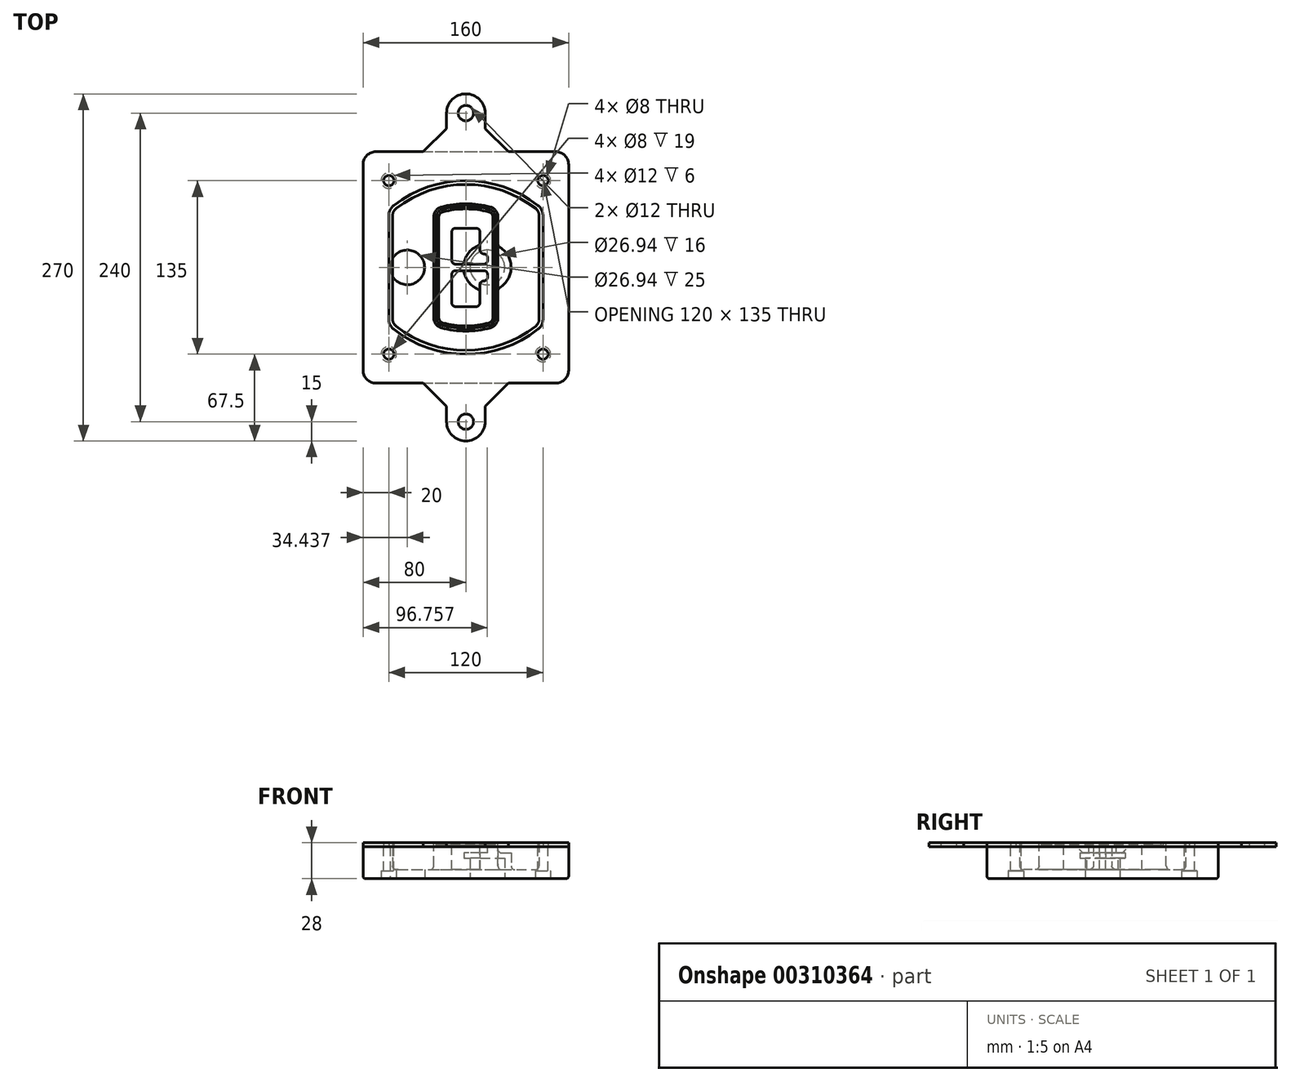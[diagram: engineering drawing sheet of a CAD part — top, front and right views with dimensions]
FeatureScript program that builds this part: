
annotation { "Feature Type Name" : "Feature", "Feature Type Description" : "" }
export const myFeature = defineFeature(function(context is Context, id is Id, definition is map)
    precondition{}
    {
        {
            var Q0;
            Q0=qCreatedBy(makeId("Top.planeOp"),FACE);
            var sketch = newSketch(context, id + "F0", { "sketchPlane" : qUnion([Q0])});
            skPoint(sketch, "E0.rect.middle", {"position": v(0, 0) * mm});
            skLineSegment(sketch, "E1.bottom", {"start": v(-70, -90) * mm, "end": v(70, -90) * mm});
            skLineSegment(sketch, "E1.top", {"start": v(-70, 90) * mm, "end": v(70, 90) * mm});
            skLineSegment(sketch, "E1.left", {"start": v(-80, -80) * mm, "end": v(-80, 80) * mm});
            skLineSegment(sketch, "E1.right", {"start": v(80, -80) * mm, "end": v(80, 80) * mm});
            skLineSegment(sketch, "E2", {"start": v(-80, 90) * mm, "end": v(80, -90) * mm, "construction": true});
            skLineSegment(sketch, "E3", {"start": v(80, 90) * mm, "end": v(-80, -90) * mm, "construction": true});
            skCircle(sketch, "E4", {"center": v(-60, 67.5) * mm, "radius": 4 * mm});
            skCircle(sketch, "E5", {"center": v(60, 67.5) * mm, "radius": 4 * mm});
            skCircle(sketch, "E6", {"center": v(60, -67.5) * mm, "radius": 4 * mm});
            skCircle(sketch, "E7", {"center": v(-60, -67.5) * mm, "radius": 4 * mm});
            skLineSegment(sketch, "E8", {"start": v(-60, 67.5) * mm, "end": v(60, 67.5) * mm, "construction": true});
            skLineSegment(sketch, "E9", {"start": v(60, 67.5) * mm, "end": v(60, -67.5) * mm, "construction": true});
            skLineSegment(sketch, "E10", {"start": v(60, -67.5) * mm, "end": v(-60, -67.5) * mm, "construction": true});
            skLineSegment(sketch, "E11", {"start": v(-60, -67.5) * mm, "end": v(-60, 67.5) * mm, "construction": true});
            skLineSegment(sketch, "E12", {"start": v(-60, 40.3) * mm, "end": v(-60, -40.3) * mm});
            skLineSegment(sketch, "E13", {"start": v(60, 40.3) * mm, "end": v(60, -40.3) * mm});
            skArc(sketch, "E14", {"start": v(56.15, 48.18) * mm, "mid": v(0, 67.5) * mm, "end": v(-56.15, 48.18) * mm});
            skArc(sketch, "E15", {"start": v(-56.15, -48.18) * mm, "mid": v(0, -67.5) * mm, "end": v(56.15, -48.18) * mm});
            skLineSegment(sketch, "E16", {"start": v(-60, 0) * mm, "end": v(60, 0) * mm, "construction": true});
            skPoint(sketch, "E17.visualSharp", {"position": v(-60, -45) * mm});
            skArc(sketch, "E17.filletArc", {"start": v(-60, -40.3) * mm, "mid": v(-58.99, -44.68) * mm, "end": v(-56.15, -48.18) * mm});
            skPoint(sketch, "E18.visualSharp", {"position": v(-60, 45) * mm});
            skArc(sketch, "E18.filletArc", {"start": v(-56.15, 48.18) * mm, "mid": v(-58.99, 44.68) * mm, "end": v(-60, 40.3) * mm});
            skPoint(sketch, "E19.visualSharp", {"position": v(60, 45) * mm});
            skArc(sketch, "E19.filletArc", {"start": v(60, 40.3) * mm, "mid": v(58.99, 44.68) * mm, "end": v(56.15, 48.18) * mm});
            skPoint(sketch, "E20.visualSharp", {"position": v(60, -45) * mm});
            skArc(sketch, "E20.filletArc", {"start": v(56.15, -48.18) * mm, "mid": v(58.99, -44.68) * mm, "end": v(60, -40.3) * mm});
            skPoint(sketch, "E21.visualSharp", {"position": v(-80, 90) * mm});
            skArc(sketch, "E21.filletArc", {"start": v(-70, 90) * mm, "mid": v(-77.07, 87.07) * mm, "end": v(-80, 80) * mm});
            skPoint(sketch, "E22.visualSharp", {"position": v(80, 90) * mm});
            skArc(sketch, "E22.filletArc", {"start": v(80, 80) * mm, "mid": v(77.07, 87.07) * mm, "end": v(70, 90) * mm});
            skPoint(sketch, "E23.visualSharp", {"position": v(80, -90) * mm});
            skArc(sketch, "E23.filletArc", {"start": v(70, -90) * mm, "mid": v(77.07, -87.07) * mm, "end": v(80, -80) * mm});
            skPoint(sketch, "E24.visualSharp", {"position": v(-80, -90) * mm});
            skArc(sketch, "E24.filletArc", {"start": v(-80, -80) * mm, "mid": v(-77.07, -87.07) * mm, "end": v(-70, -90) * mm});
            skArc(sketch, "E25.0", {"start": v(57, 40.3) * mm, "mid": v(56.3, 43.36) * mm, "end": v(54.3, 45.81) * mm});
            skLineSegment(sketch, "E25.1", {"start": v(57, 40.3) * mm, "end": v(57, -40.3) * mm});
            skArc(sketch, "E25.2", {"start": v(54.3, -45.81) * mm, "mid": v(56.3, -43.36) * mm, "end": v(57, -40.3) * mm});
            skArc(sketch, "E25.3", {"start": v(-54.3, -45.81) * mm, "mid": v(0, -64.5) * mm, "end": v(54.3, -45.81) * mm});
            skArc(sketch, "E25.4", {"start": v(-57, -40.3) * mm, "mid": v(-56.3, -43.36) * mm, "end": v(-54.3, -45.81) * mm});
            skArc(sketch, "E25.5", {"start": v(54.3, 45.81) * mm, "mid": v(0, 64.5) * mm, "end": v(-54.3, 45.81) * mm});
            skLineSegment(sketch, "E25.6", {"start": v(-57, 40.3) * mm, "end": v(-57, -40.3) * mm});
            skArc(sketch, "E25.7", {"start": v(-54.3, 45.81) * mm, "mid": v(-56.3, 43.36) * mm, "end": v(-57, 40.3) * mm});
            skArc(sketch, "E26.0", {"start": v(-58.62, 51.33) * mm, "mid": v(-62.58, 46.43) * mm, "end": v(-64, 40.3) * mm});
            skArc(sketch, "E26.1", {"start": v(58.62, 51.33) * mm, "mid": v(0, 71.5) * mm, "end": v(-58.62, 51.33) * mm});
            skArc(sketch, "E26.2", {"start": v(64, 40.3) * mm, "mid": v(62.58, 46.43) * mm, "end": v(58.62, 51.33) * mm});
            skLineSegment(sketch, "E26.3", {"start": v(64, 40.3) * mm, "end": v(64, -40.3) * mm});
            skArc(sketch, "E26.4", {"start": v(58.62, -51.33) * mm, "mid": v(62.58, -46.43) * mm, "end": v(64, -40.3) * mm});
            skLineSegment(sketch, "E26.5", {"start": v(-64, 40.3) * mm, "end": v(-64, -40.3) * mm});
            skArc(sketch, "E26.6", {"start": v(-58.62, -51.33) * mm, "mid": v(0, -71.5) * mm, "end": v(58.62, -51.33) * mm});
            skArc(sketch, "E26.7", {"start": v(-64, -40.3) * mm, "mid": v(-62.58, -46.43) * mm, "end": v(-58.62, -51.33) * mm});
            skSolve(sketch);
        }
        {
            var Q0;
            Q0=makeQuery(id+"F0.imprint","IMPRINT",FACE,{"disambiguationData":[TD([[makeQuery(id+"F0.imprint","IMPRINT",EDGE,{"derivedFrom":sQuery(id+"F0.wireOp",EDGE,"E1.bottom")}),1.0]])]});
            var Q1;
            Q1=makeQuery(id+"F0.imprint","IMPRINT",FACE,{"disambiguationData":[TD([[makeQuery(id+"F0.imprint","IMPRINT",EDGE,{"derivedFrom":sQuery(id+"F0.wireOp",EDGE,"E12")}),1.0]])]});
            var Q2;
            Q2=makeQuery(id+"F0.imprint","IMPRINT",FACE,{"disambiguationData":[TD([[makeQuery(id+"F0.imprint","IMPRINT",EDGE,{"derivedFrom":sQuery(id+"F0.wireOp",EDGE,"E25.0")}),1.0]])]});
            var Q3;
            Q3=makeQuery(id+"F0.imprint","IMPRINT",FACE,{"disambiguationData":[TD([[makeQuery(id+"F0.imprint","IMPRINT",EDGE,{"derivedFrom":sQuery(id+"F0.wireOp",EDGE,"E12")}),-1.0]])]});
            extrude(context, id + "F1", {"entities" : qUnion([Q0, Q1, Q2, Q3]), "oppositeDirection" : true, "depth" : 25 * mm});
        }
        {
            var Q0;
            Q0=makeQuery(id+"F0.imprint","IMPRINT",FACE,{"disambiguationData":[TD([[makeQuery(id+"F0.imprint","IMPRINT",EDGE,{"derivedFrom":sQuery(id+"F0.wireOp",EDGE,"E12")}),1.0]])]});
            extrude(context, id + "F2", {"entities" : qUnion([Q0]), "operationType" : NewBodyOperationType.ADD, "depth" : 3 * mm});
        }
        {
            var Q0;
            Q0=makeQuery(id+"F0.imprint","IMPRINT",FACE,{"disambiguationData":[TD([[makeQuery(id+"F0.imprint","IMPRINT",EDGE,{"derivedFrom":sQuery(id+"F0.wireOp",EDGE,"E25.0")}),1.0]])]});
            extrude(context, id + "F3", {"entities" : qUnion([Q0]), "operationType" : NewBodyOperationType.REMOVE, "oppositeDirection" : true, "depth" : 18 * mm});
        }
        {
            var Q0;
            Q0=makeQuery(id+"F2.opExtrude","CAP_FACE",FACE,{"disambiguationData":[OSD([sQuery(id+"F0.wireOp",EDGE,"E12"),sQuery(id+"F0.wireOp",EDGE,"E13"),sQuery(id+"F0.wireOp",EDGE,"E14"),sQuery(id+"F0.wireOp",EDGE,"E15"),sQuery(id+"F0.wireOp",EDGE,"E17.filletArc"),sQuery(id+"F0.wireOp",EDGE,"E18.filletArc"),sQuery(id+"F0.wireOp",EDGE,"E19.filletArc"),sQuery(id+"F0.wireOp",EDGE,"E20.filletArc"),sQuery(id+"F0.wireOp",EDGE,"E25.0"),sQuery(id+"F0.wireOp",EDGE,"E25.1"),sQuery(id+"F0.wireOp",EDGE,"E25.2"),sQuery(id+"F0.wireOp",EDGE,"E25.3"),sQuery(id+"F0.wireOp",EDGE,"E25.4"),sQuery(id+"F0.wireOp",EDGE,"E25.5"),sQuery(id+"F0.wireOp",EDGE,"E25.6"),sQuery(id+"F0.wireOp",EDGE,"E25.7")])],"isStart":false});
            var sketch = newSketch(context, id + "F4", { "sketchPlane" : qUnion([Q0])});
            skArc(sketch, "E27.0", {"start": v(-19.08, -46.97) * mm, "mid": v(0, -49.5) * mm, "end": v(19.08, -46.97) * mm});
            skArc(sketch, "E28.0", {"start": v(19.08, 46.97) * mm, "mid": v(0, 49.5) * mm, "end": v(-19.08, 46.97) * mm});
            skLineSegment(sketch, "E29", {"start": v(-25, 39.25) * mm, "end": v(-25, -39.25) * mm});
            skLineSegment(sketch, "E30", {"start": v(25, 39.25) * mm, "end": v(25, -39.25) * mm});
            skLineSegment(sketch, "E31", {"start": v(-25, 45.1) * mm, "end": v(25, 45.1) * mm, "construction": true});
            skLineSegment(sketch, "E32", {"start": v(-25, -45.1) * mm, "end": v(25, -45.1) * mm, "construction": true});
            skPoint(sketch, "E33.visualSharp", {"position": v(-25, 45.1) * mm});
            skArc(sketch, "E33.filletArc", {"start": v(-19.08, 46.97) * mm, "mid": v(-23.35, 44.11) * mm, "end": v(-25, 39.25) * mm});
            skPoint(sketch, "E34.visualSharp", {"position": v(25, 45.1) * mm});
            skArc(sketch, "E34.filletArc", {"start": v(25, 39.25) * mm, "mid": v(23.35, 44.11) * mm, "end": v(19.08, 46.97) * mm});
            skPoint(sketch, "E35.visualSharp", {"position": v(25, -45.1) * mm});
            skArc(sketch, "E35.filletArc", {"start": v(19.08, -46.97) * mm, "mid": v(23.35, -44.11) * mm, "end": v(25, -39.25) * mm});
            skPoint(sketch, "E36.visualSharp", {"position": v(-25, -45.1) * mm});
            skArc(sketch, "E36.filletArc", {"start": v(-25, -39.25) * mm, "mid": v(-23.35, -44.11) * mm, "end": v(-19.08, -46.97) * mm});
            skArc(sketch, "E37.0", {"start": v(54.3, 45.81) * mm, "mid": v(0, 64.5) * mm, "end": v(-54.3, 45.81) * mm});
            skArc(sketch, "E37.1", {"start": v(-54.3, 45.81) * mm, "mid": v(-56.3, 43.36) * mm, "end": v(-57, 40.3) * mm});
            skLineSegment(sketch, "E37.2", {"start": v(-57, 40.3) * mm, "end": v(-57, -40.3) * mm});
            skArc(sketch, "E37.3", {"start": v(-57, -40.3) * mm, "mid": v(-56.3, -43.36) * mm, "end": v(-54.3, -45.81) * mm});
            skArc(sketch, "E37.4", {"start": v(-54.3, -45.81) * mm, "mid": v(0, -64.5) * mm, "end": v(54.3, -45.81) * mm});
            skArc(sketch, "E37.5", {"start": v(54.3, -45.81) * mm, "mid": v(56.3, -43.36) * mm, "end": v(57, -40.3) * mm});
            skLineSegment(sketch, "E37.6", {"start": v(57, 40.3) * mm, "end": v(57, -40.3) * mm});
            skArc(sketch, "E37.7", {"start": v(57, 40.3) * mm, "mid": v(56.3, 43.36) * mm, "end": v(54.3, 45.81) * mm});
            skLineSegment(sketch, "E38.0", {"start": v(23, 39.25) * mm, "end": v(23, -39.25) * mm});
            skArc(sketch, "E38.1", {"start": v(18.56, -45.04) * mm, "mid": v(21.76, -42.9) * mm, "end": v(23, -39.25) * mm});
            skArc(sketch, "E38.2", {"start": v(-18.56, -45.04) * mm, "mid": v(0, -47.5) * mm, "end": v(18.56, -45.04) * mm});
            skArc(sketch, "E38.3", {"start": v(-23, -39.25) * mm, "mid": v(-21.76, -42.9) * mm, "end": v(-18.56, -45.04) * mm});
            skLineSegment(sketch, "E38.4", {"start": v(-23, 39.25) * mm, "end": v(-23, -39.25) * mm});
            skArc(sketch, "E38.5", {"start": v(23, 39.25) * mm, "mid": v(21.76, 42.9) * mm, "end": v(18.56, 45.04) * mm});
            skArc(sketch, "E38.6", {"start": v(-18.56, 45.04) * mm, "mid": v(-21.76, 42.9) * mm, "end": v(-23, 39.25) * mm});
            skArc(sketch, "E38.7", {"start": v(18.56, 45.04) * mm, "mid": v(0, 47.5) * mm, "end": v(-18.56, 45.04) * mm});
            skArc(sketch, "E39.0", {"start": v(21, 39.25) * mm, "mid": v(20.18, 41.68) * mm, "end": v(18.04, 43.1) * mm});
            skLineSegment(sketch, "E39.1", {"start": v(21, 39.25) * mm, "end": v(21, -39.25) * mm});
            skArc(sketch, "E39.2", {"start": v(18.04, -43.1) * mm, "mid": v(20.18, -41.68) * mm, "end": v(21, -39.25) * mm});
            skArc(sketch, "E39.3", {"start": v(-18.04, -43.1) * mm, "mid": v(0, -45.5) * mm, "end": v(18.04, -43.1) * mm});
            skArc(sketch, "E39.4", {"start": v(-21, -39.25) * mm, "mid": v(-20.18, -41.68) * mm, "end": v(-18.04, -43.1) * mm});
            skArc(sketch, "E39.5", {"start": v(18.04, 43.1) * mm, "mid": v(0, 45.5) * mm, "end": v(-18.04, 43.1) * mm});
            skLineSegment(sketch, "E39.6", {"start": v(-21, 39.25) * mm, "end": v(-21, -39.25) * mm});
            skArc(sketch, "E39.7", {"start": v(-18.04, 43.1) * mm, "mid": v(-20.18, 41.68) * mm, "end": v(-21, 39.25) * mm});
            skLineSegment(sketch, "E40", {"start": v(-25, 0) * mm, "end": v(25, 0) * mm, "construction": true});
            skLineSegment(sketch, "E41", {"start": v(-11, 5.5) * mm, "end": v(-11, 27.5) * mm});
            skLineSegment(sketch, "E42", {"start": v(-8, 30.5) * mm, "end": v(8, 30.5) * mm});
            skLineSegment(sketch, "E43", {"start": v(11, 27.5) * mm, "end": v(11, 13.5) * mm});
            skLineSegment(sketch, "E44", {"start": v(14, 10.5) * mm, "end": v(14, 10.5) * mm});
            skLineSegment(sketch, "E45", {"start": v(17, 7.5) * mm, "end": v(17, 5.5) * mm});
            skLineSegment(sketch, "E46", {"start": v(14, 2.5) * mm, "end": v(-8, 2.5) * mm});
            skPoint(sketch, "E47.visualSharp", {"position": v(-11, 30.5) * mm});
            skArc(sketch, "E47.filletArc", {"start": v(-8, 30.5) * mm, "mid": v(-10.12, 29.62) * mm, "end": v(-11, 27.5) * mm});
            skPoint(sketch, "E48.visualSharp", {"position": v(11, 30.5) * mm});
            skArc(sketch, "E48.filletArc", {"start": v(11, 27.5) * mm, "mid": v(10.12, 29.62) * mm, "end": v(8, 30.5) * mm});
            skPoint(sketch, "E49.visualSharp", {"position": v(11, 10.5) * mm});
            skArc(sketch, "E49.filletArc", {"start": v(11, 13.5) * mm, "mid": v(11.88, 11.38) * mm, "end": v(14, 10.5) * mm});
            skPoint(sketch, "E50.visualSharp", {"position": v(17, 10.5) * mm});
            skArc(sketch, "E50.filletArc", {"start": v(17, 7.5) * mm, "mid": v(16.12, 9.62) * mm, "end": v(14, 10.5) * mm});
            skPoint(sketch, "E51.visualSharp", {"position": v(17, 2.5) * mm});
            skArc(sketch, "E51.filletArc", {"start": v(14, 2.5) * mm, "mid": v(16.12, 3.38) * mm, "end": v(17, 5.5) * mm});
            skPoint(sketch, "E52.visualSharp", {"position": v(-11, 2.5) * mm});
            skArc(sketch, "E52.filletArc", {"start": v(-11, 5.5) * mm, "mid": v(-10.12, 3.38) * mm, "end": v(-8, 2.5) * mm});
            skLineSegment(sketch, "E53.0.MirrorCS", {"start": v(14, -2.5) * mm, "end": v(-8, -2.5) * mm});
            skArc(sketch, "E54.0.MirrorCS", {"start": v(-11, -5.5) * mm, "mid": v(-10.12, -3.38) * mm, "end": v(-8, -2.5) * mm});
            skLineSegment(sketch, "E55.0.MirrorCS", {"start": v(-11, -5.5) * mm, "end": v(-11, -27.5) * mm});
            skArc(sketch, "E56.0.MirrorCS", {"start": v(-8, -30.5) * mm, "mid": v(-10.12, -29.62) * mm, "end": v(-11, -27.5) * mm});
            skLineSegment(sketch, "E57.0.MirrorCS", {"start": v(-8, -30.5) * mm, "end": v(8, -30.5) * mm});
            skArc(sketch, "E58.0.MirrorCS", {"start": v(11, -27.5) * mm, "mid": v(10.12, -29.62) * mm, "end": v(8, -30.5) * mm});
            skLineSegment(sketch, "E59.0.MirrorCS", {"start": v(11, -27.5) * mm, "end": v(11, -13.5) * mm});
            skArc(sketch, "E60.0.MirrorCS", {"start": v(11, -13.5) * mm, "mid": v(11.88, -11.38) * mm, "end": v(14, -10.5) * mm});
            skArc(sketch, "E61.0.MirrorCS", {"start": v(17, -7.5) * mm, "mid": v(16.12, -9.62) * mm, "end": v(14, -10.5) * mm});
            skLineSegment(sketch, "E62.0.MirrorCS", {"start": v(17, -7.5) * mm, "end": v(17, -5.5) * mm});
            skArc(sketch, "E63.0.MirrorCS", {"start": v(14, -2.5) * mm, "mid": v(16.12, -3.38) * mm, "end": v(17, -5.5) * mm});
            skSolve(sketch);
        }
        {
            var Q0;
            Q0=makeQuery(id+"F4.imprint","IMPRINT",FACE,{"disambiguationData":[TD([[makeQuery(id+"F4.imprint","IMPRINT",EDGE,{"derivedFrom":sQuery(id+"F4.wireOp",EDGE,"E27.0")}),1.0]])]});
            var Q1;
            Q1=makeQuery(id+"F4.imprint","IMPRINT",FACE,{"disambiguationData":[TD([[makeQuery(id+"F4.imprint","IMPRINT",EDGE,{"derivedFrom":sQuery(id+"F4.wireOp",EDGE,"E38.0")}),-1.0]])]});
            var Q2;
            Q2=makeQuery(id+"F4.imprint","IMPRINT",FACE,{"disambiguationData":[TD([[makeQuery(id+"F4.imprint","IMPRINT",EDGE,{"derivedFrom":sQuery(id+"F4.wireOp",EDGE,"E39.0")}),1.0]])]});
            extrude(context, id + "F5", {"entities" : qUnion([Q0, Q1, Q2]), "operationType" : NewBodyOperationType.ADD, "endBound" : BoundingType.UP_TO_NEXT, "oppositeDirection" : true, "depth" : 25 * mm});
        }
        {
            var Q0;
            Q0=makeQuery(id+"F4.imprint","IMPRINT",FACE,{"disambiguationData":[TD([[makeQuery(id+"F4.imprint","IMPRINT",EDGE,{"derivedFrom":sQuery(id+"F4.wireOp",EDGE,"E38.0")}),-1.0]])]});
            extrude(context, id + "F6", {"entities" : qUnion([Q0]), "operationType" : NewBodyOperationType.REMOVE, "oppositeDirection" : true, "depth" : 2 * mm});
        }
        {
            var Q0;
            Q0=makeQuery(id+"F1.opExtrude","CAP_FACE",FACE,{"disambiguationData":[OSD([sQuery(id+"F0.wireOp",EDGE,"E1.bottom"),sQuery(id+"F0.wireOp",EDGE,"E1.top"),sQuery(id+"F0.wireOp",EDGE,"E1.left"),sQuery(id+"F0.wireOp",EDGE,"E1.right"),sQuery(id+"F0.wireOp",EDGE,"E4"),sQuery(id+"F0.wireOp",EDGE,"E5"),sQuery(id+"F0.wireOp",EDGE,"E6"),sQuery(id+"F0.wireOp",EDGE,"E7"),sQuery(id+"F0.wireOp",EDGE,"E21.filletArc"),sQuery(id+"F0.wireOp",EDGE,"E22.filletArc"),sQuery(id+"F0.wireOp",EDGE,"E23.filletArc"),sQuery(id+"F0.wireOp",EDGE,"E24.filletArc")])],"isStart":false});
            var sketch = newSketch(context, id + "F7", { "sketchPlane" : qUnion([Q0])});
            skCircle(sketch, "E64", {"center": v(16.76, 0) * mm, "radius": 13.47 * mm});
            skCircle(sketch, "E65", {"center": v(-45.56, 0) * mm, "radius": 13.47 * mm});
            skLineSegment(sketch, "E66", {"start": v(80, 0) * mm, "end": v(-80, 0) * mm});
            skCircle(sketch, "E67", {"center": v(16.76, 0) * mm, "radius": 18.47 * mm});
            skCircle(sketch, "E68", {"center": v(60, -67.5) * mm, "radius": 6 * mm});
            skCircle(sketch, "E69", {"center": v(-60, -67.5) * mm, "radius": 6 * mm});
            skCircle(sketch, "E70", {"center": v(-60, 67.5) * mm, "radius": 6 * mm});
            skCircle(sketch, "E71", {"center": v(60, 67.5) * mm, "radius": 6 * mm});
            skSolve(sketch);
        }
        {
            var Q0;
            {var subQ1=sQuery(id+"F7.wireOp",EDGE,"E66");var subQ4=sQuery(id+"F7.wireOp",EDGE,"E64");var subQ6=makeQuery(id+"F7.imprint","INTERSECT",VERTEX,{"disambiguationData":[OD(0.0)],"derivedFrom":[subQ4,subQ1]});Q0=makeQuery(id+"F7.imprint","IMPRINT",FACE,{"disambiguationData":[TD([[makeQuery(id+"F7.imprint","IMPRINT",EDGE,{"disambiguationData":[TD([[subQ6,-1.0]])],"derivedFrom":subQ4}),-1.0]])]});}
            var Q1;
            {var subQ0=sQuery(id+"F7.wireOp",EDGE,"E66");var subQ1=sQuery(id+"F7.wireOp",EDGE,"E64");var subQ3=makeQuery(id+"F7.imprint","INTERSECT",VERTEX,{"disambiguationData":[OD(0.0)],"derivedFrom":[subQ1,subQ0]});Q1=makeQuery(id+"F7.imprint","IMPRINT",FACE,{"disambiguationData":[TD([[makeQuery(id+"F7.imprint","IMPRINT",EDGE,{"disambiguationData":[TD([[subQ3,-1.0]])],"derivedFrom":subQ1}),1.0]])]});}
            var Q2;
            {var subQ0=sQuery(id+"F7.wireOp",EDGE,"E66");var subQ1=sQuery(id+"F7.wireOp",EDGE,"E64");var subQ3=makeQuery(id+"F7.imprint","INTERSECT",VERTEX,{"disambiguationData":[OD(0.0)],"derivedFrom":[subQ1,subQ0]});Q2=makeQuery(id+"F7.imprint","IMPRINT",FACE,{"disambiguationData":[TD([[makeQuery(id+"F7.imprint","IMPRINT",EDGE,{"disambiguationData":[TD([[subQ3,1.0]])],"derivedFrom":subQ1}),1.0]])]});}
            var Q3;
            {var subQ1=sQuery(id+"F7.wireOp",EDGE,"E66");var subQ4=sQuery(id+"F7.wireOp",EDGE,"E64");var subQ6=makeQuery(id+"F7.imprint","INTERSECT",VERTEX,{"disambiguationData":[OD(0.0)],"derivedFrom":[subQ4,subQ1]});Q3=makeQuery(id+"F7.imprint","IMPRINT",FACE,{"disambiguationData":[TD([[makeQuery(id+"F7.imprint","IMPRINT",EDGE,{"disambiguationData":[TD([[subQ6,1.0]])],"derivedFrom":subQ4}),-1.0]])]});}
            extrude(context, id + "F8", {"entities" : qUnion([Q0, Q1, Q2, Q3]), "operationType" : NewBodyOperationType.ADD, "oppositeDirection" : true, "depth" : 20 * mm});
        }
        {
            var Q0;
            {var subQ0=sQuery(id+"F7.wireOp",EDGE,"E66");var subQ1=sQuery(id+"F7.wireOp",EDGE,"E64");var subQ3=makeQuery(id+"F7.imprint","INTERSECT",VERTEX,{"disambiguationData":[OD(0.0)],"derivedFrom":[subQ1,subQ0]});Q0=makeQuery(id+"F7.imprint","IMPRINT",FACE,{"disambiguationData":[TD([[makeQuery(id+"F7.imprint","IMPRINT",EDGE,{"disambiguationData":[TD([[subQ3,-1.0]])],"derivedFrom":subQ1}),1.0]])]});}
            var Q1;
            {var subQ0=sQuery(id+"F7.wireOp",EDGE,"E66");var subQ1=sQuery(id+"F7.wireOp",EDGE,"E64");var subQ3=makeQuery(id+"F7.imprint","INTERSECT",VERTEX,{"disambiguationData":[OD(0.0)],"derivedFrom":[subQ1,subQ0]});Q1=makeQuery(id+"F7.imprint","IMPRINT",FACE,{"disambiguationData":[TD([[makeQuery(id+"F7.imprint","IMPRINT",EDGE,{"disambiguationData":[TD([[subQ3,1.0]])],"derivedFrom":subQ1}),1.0]])]});}
            extrude(context, id + "F9", {"entities" : qUnion([Q0, Q1]), "operationType" : NewBodyOperationType.REMOVE, "oppositeDirection" : true, "depth" : 16 * mm});
        }
        {
            var Q0;
            {var subQ0=sQuery(id+"F7.wireOp",EDGE,"E66");var subQ1=sQuery(id+"F7.wireOp",EDGE,"E65");var subQ3=makeQuery(id+"F7.imprint","INTERSECT",VERTEX,{"disambiguationData":[OD(0.0)],"derivedFrom":[subQ1,subQ0]});Q0=makeQuery(id+"F7.imprint","IMPRINT",FACE,{"disambiguationData":[TD([[makeQuery(id+"F7.imprint","IMPRINT",EDGE,{"disambiguationData":[TD([[subQ3,-1.0]])],"derivedFrom":subQ1}),1.0]])]});}
            var Q1;
            {var subQ0=sQuery(id+"F7.wireOp",EDGE,"E66");var subQ1=sQuery(id+"F7.wireOp",EDGE,"E65");var subQ3=makeQuery(id+"F7.imprint","INTERSECT",VERTEX,{"disambiguationData":[OD(0.0)],"derivedFrom":[subQ1,subQ0]});Q1=makeQuery(id+"F7.imprint","IMPRINT",FACE,{"disambiguationData":[TD([[makeQuery(id+"F7.imprint","IMPRINT",EDGE,{"disambiguationData":[TD([[subQ3,1.0]])],"derivedFrom":subQ1}),1.0]])]});}
            extrude(context, id + "F10", {"entities" : qUnion([Q0, Q1]), "operationType" : NewBodyOperationType.REMOVE, "oppositeDirection" : true, "depth" : 25 * mm});
        }
        {
            var Q0;
            Q0=makeQuery(id+"F7.imprint","IMPRINT",FACE,{"disambiguationData":[TD([[makeQuery(id+"F7.imprint","IMPRINT",EDGE,{"derivedFrom":sQuery(id+"F7.wireOp",EDGE,"E68")}),1.0]])]});
            var Q1;
            Q1=makeQuery(id+"F7.imprint","IMPRINT",FACE,{"disambiguationData":[TD([[makeQuery(id+"F7.imprint","IMPRINT",EDGE,{"derivedFrom":makeQuery(id+"F1.opExtrude","CAP_EDGE",EDGE,{"disambiguationData":[OSD([sQuery(id+"F0.wireOp",EDGE,"E5")])],"isStart":false})}),-1.0]])]});
            var Q2;
            Q2=makeQuery(id+"F7.imprint","IMPRINT",FACE,{"disambiguationData":[TD([[makeQuery(id+"F7.imprint","IMPRINT",EDGE,{"derivedFrom":sQuery(id+"F7.wireOp",EDGE,"E69")}),1.0]])]});
            var Q3;
            Q3=makeQuery(id+"F7.imprint","IMPRINT",FACE,{"disambiguationData":[TD([[makeQuery(id+"F7.imprint","IMPRINT",EDGE,{"derivedFrom":makeQuery(id+"F1.opExtrude","CAP_EDGE",EDGE,{"disambiguationData":[OSD([sQuery(id+"F0.wireOp",EDGE,"E4")])],"isStart":false})}),-1.0]])]});
            var Q4;
            Q4=makeQuery(id+"F7.imprint","IMPRINT",FACE,{"disambiguationData":[TD([[makeQuery(id+"F7.imprint","IMPRINT",EDGE,{"derivedFrom":sQuery(id+"F7.wireOp",EDGE,"E70")}),1.0]])]});
            var Q5;
            Q5=makeQuery(id+"F7.imprint","IMPRINT",FACE,{"disambiguationData":[TD([[makeQuery(id+"F7.imprint","IMPRINT",EDGE,{"derivedFrom":makeQuery(id+"F1.opExtrude","CAP_EDGE",EDGE,{"disambiguationData":[OSD([sQuery(id+"F0.wireOp",EDGE,"E7")])],"isStart":false})}),-1.0]])]});
            var Q6;
            Q6=makeQuery(id+"F7.imprint","IMPRINT",FACE,{"disambiguationData":[TD([[makeQuery(id+"F7.imprint","IMPRINT",EDGE,{"derivedFrom":sQuery(id+"F7.wireOp",EDGE,"E71")}),1.0]])]});
            var Q7;
            Q7=makeQuery(id+"F7.imprint","IMPRINT",FACE,{"disambiguationData":[TD([[makeQuery(id+"F7.imprint","IMPRINT",EDGE,{"derivedFrom":makeQuery(id+"F1.opExtrude","CAP_EDGE",EDGE,{"disambiguationData":[OSD([sQuery(id+"F0.wireOp",EDGE,"E6")])],"isStart":false})}),-1.0]])]});
            extrude(context, id + "F11", {"entities" : qUnion([Q0, Q1, Q2, Q3, Q4, Q5, Q6, Q7]), "operationType" : NewBodyOperationType.REMOVE, "oppositeDirection" : true, "depth" : 6 * mm});
        }
        {
            var Q0;
            Q0=makeQuery(id+"F9.boolean.opBoolean","COPY",FACE,{"derivedFrom":makeQuery(id+"F9.opExtrude","CAP_FACE",FACE,{"disambiguationData":[OSD([sQuery(id+"F7.wireOp",EDGE,"E64")])],"isStart":false})});
            var sketch = newSketch(context, id + "F12", { "sketchPlane" : qUnion([Q0])});
            skArc(sketch, "E72.0", {"start": v(11, 17.55) * mm, "mid": v(2.57, 11.82) * mm, "end": v(-1.54, 2.5) * mm});
            skArc(sketch, "E72.1", {"start": v(-1.54, -2.5) * mm, "mid": v(2.57, -11.82) * mm, "end": v(11, -17.55) * mm});
            skLineSegment(sketch, "E73", {"start": v(-1.54, -2.5) * mm, "end": v(14, -2.5) * mm});
            skLineSegment(sketch, "E74.0", {"start": v(14, 2.5) * mm, "end": v(-1.54, 2.5) * mm});
            skArc(sketch, "E74.1", {"start": v(14, 2.5) * mm, "mid": v(16.12, 3.38) * mm, "end": v(17, 5.5) * mm});
            skLineSegment(sketch, "E74.2", {"start": v(17, 7.5) * mm, "end": v(17, 5.5) * mm});
            skArc(sketch, "E74.3", {"start": v(17, 7.5) * mm, "mid": v(16.12, 9.62) * mm, "end": v(14, 10.5) * mm});
            skArc(sketch, "E74.4", {"start": v(11, 13.5) * mm, "mid": v(11.88, 11.38) * mm, "end": v(14, 10.5) * mm});
            skLineSegment(sketch, "E74.5", {"start": v(11, 17.55) * mm, "end": v(11, 13.5) * mm});
            skLineSegment(sketch, "E74.7", {"start": v(14, -2.5) * mm, "end": v(-1.54, -2.5) * mm});
            skArc(sketch, "E74.8", {"start": v(14, -2.5) * mm, "mid": v(16.12, -3.38) * mm, "end": v(17, -5.5) * mm});
            skLineSegment(sketch, "E74.9", {"start": v(17, -7.5) * mm, "end": v(17, -5.5) * mm});
            skArc(sketch, "E74.10", {"start": v(17, -7.5) * mm, "mid": v(16.12, -9.62) * mm, "end": v(14, -10.5) * mm});
            skArc(sketch, "E74.11", {"start": v(11, -13.5) * mm, "mid": v(11.88, -11.38) * mm, "end": v(14, -10.5) * mm});
            skLineSegment(sketch, "E74.12", {"start": v(11, -17.55) * mm, "end": v(11, -13.5) * mm});
            skPoint(sketch, "E75.orphan", {"position": v(11, -27.5) * mm});
            skPoint(sketch, "E76.orphan", {"position": v(-8, -2.5) * mm});
            skPoint(sketch, "E77.orphan", {"position": v(-8, 2.5) * mm});
            skPoint(sketch, "E78.orphan", {"position": v(11, 27.5) * mm});
            skSolve(sketch);
        }
        {
            var Q0;
            {var subQ7=sQuery(id+"F12.wireOp",EDGE,"E72.0");var subQ14=sQuery(id+"F12.wireOp",EDGE,"E72.1");var subQ16=sQuery(id+"F12.wireOp",EDGE,"E74.1");var subQ18=sQuery(id+"F12.wireOp",EDGE,"E74.8");Q0=qUnion([makeQuery(id+"F12.imprint","IMPRINT",FACE,{"disambiguationData":[TD([[makeQuery(id+"F12.imprint","IMPRINT",EDGE,{"derivedFrom":subQ7}),1.0]])]}),makeQuery(id+"F12.imprint","IMPRINT",FACE,{"disambiguationData":[TD([[makeQuery(id+"F12.imprint","IMPRINT",EDGE,{"derivedFrom":subQ14}),1.0]])]}),makeQuery(id+"F12.imprint","IMPRINT",FACE,{"disambiguationData":[TD([[makeQuery(id+"F12.imprint","IMPRINT",EDGE,{"derivedFrom":subQ16}),1.0]])]}),makeQuery(id+"F12.imprint","IMPRINT",FACE,{"disambiguationData":[TD([[makeQuery(id+"F12.imprint","IMPRINT",EDGE,{"derivedFrom":subQ18}),-1.0]])]})]);}
            var Q1;
            Q1=makeQuery(id+"F5.boolean.opBoolean","SPLIT",FACE,{"disambiguationData":[TD([makeQuery(id+"F5.opExtrude","SWEPT_FACE",FACE,{"disambiguationData":[OSD([sQuery(id+"F4.wireOp",EDGE,"E41")])]})])],"derivedFrom":makeQuery(id+"F3.boolean.opBoolean","COPY",FACE,{"derivedFrom":makeQuery(id+"F3.opExtrude","CAP_FACE",FACE,{"disambiguationData":[OSD([sQuery(id+"F0.wireOp",EDGE,"E25.0"),sQuery(id+"F0.wireOp",EDGE,"E25.1"),sQuery(id+"F0.wireOp",EDGE,"E25.2"),sQuery(id+"F0.wireOp",EDGE,"E25.3"),sQuery(id+"F0.wireOp",EDGE,"E25.4"),sQuery(id+"F0.wireOp",EDGE,"E25.5"),sQuery(id+"F0.wireOp",EDGE,"E25.6"),sQuery(id+"F0.wireOp",EDGE,"E25.7")])],"isStart":false})})});
            extrude(context, id + "F13", {"entities" : qUnion([Q0]), "operationType" : NewBodyOperationType.REMOVE, "endBound" : BoundingType.UP_TO_SURFACE, "endBoundEntityFace" : qUnion([Q1]), "depth" : 25 * mm});
        }
        {
            var Q0;
            Q0=makeQuery(id+"F3.boolean.opBoolean","COPY",EDGE,{"derivedFrom":makeQuery(id+"F3.opExtrude","CAP_EDGE",EDGE,{"disambiguationData":[OSD([sQuery(id+"F0.wireOp",EDGE,"E25.6")])],"isStart":false})});
            var Q1;
            Q1=makeQuery(id+"F8.boolean.opBoolean","INTERSECT",EDGE,{"derivedFrom":[makeQuery(id+"F5.opExtrude","SWEPT_FACE",FACE,{"disambiguationData":[OSD([sQuery(id+"F4.wireOp",EDGE,"E30")])]}),makeQuery(id+"F8.opExtrude","CAP_FACE",FACE,{"disambiguationData":[OSD([sQuery(id+"F7.wireOp",EDGE,"E67")])],"isStart":false})]});
            var Q2;
            Q2=makeQuery(id+"F8.boolean.opBoolean","INTERSECT",EDGE,{"disambiguationData":[OD(1.0)],"derivedFrom":[makeQuery(id+"F5.opExtrude","SWEPT_FACE",FACE,{"disambiguationData":[OSD([sQuery(id+"F4.wireOp",EDGE,"E30")])]}),makeQuery(id+"F8.opExtrude","SWEPT_FACE",FACE,{"disambiguationData":[OSD([sQuery(id+"F7.wireOp",EDGE,"E67")])]})]});
            var Q3;
            {var subQ0=sQuery(id+"F4.wireOp",EDGE,"E30");Q3=makeQuery(id+"F8.boolean.opBoolean","SPLIT",EDGE,{"disambiguationData":[TD([makeQuery(id+"F5.opExtrude","SWEPT_FACE",FACE,{"disambiguationData":[OSD([sQuery(id+"F4.wireOp",EDGE,"E35.filletArc")])]})])],"derivedFrom":makeQuery(id+"F5.opExtrude","CAP_EDGE",EDGE,{"disambiguationData":[OSD([subQ0])],"isStart":false})});}
            var Q4;
            {var subQ0=sQuery(id+"F0.wireOp",EDGE,"E25.7");var subQ1=sQuery(id+"F0.wireOp",EDGE,"E25.1");var subQ2=sQuery(id+"F0.wireOp",EDGE,"E25.6");var subQ3=sQuery(id+"F0.wireOp",EDGE,"E25.5");var subQ4=sQuery(id+"F0.wireOp",EDGE,"E25.4");var subQ5=sQuery(id+"F0.wireOp",EDGE,"E25.0");var subQ6=sQuery(id+"F0.wireOp",EDGE,"E25.2");var subQ7=sQuery(id+"F0.wireOp",EDGE,"E25.3");Q4=makeQuery(id+"F8.boolean.opBoolean","INTERSECT",EDGE,{"derivedFrom":[makeQuery(id+"F5.boolean.opBoolean","SPLIT",FACE,{"disambiguationData":[TD([makeQuery(id+"F2.opExtrude","SWEPT_FACE",FACE,{"disambiguationData":[OSD([subQ5])]})])],"derivedFrom":makeQuery(id+"F3.boolean.opBoolean","COPY",FACE,{"derivedFrom":makeQuery(id+"F3.opExtrude","CAP_FACE",FACE,{"disambiguationData":[OSD([subQ5,subQ1,subQ6,subQ7,subQ4,subQ3,subQ2,subQ0])],"isStart":false})})}),makeQuery(id+"F8.opExtrude","SWEPT_FACE",FACE,{"disambiguationData":[OSD([sQuery(id+"F7.wireOp",EDGE,"E67")])]})]});}
            var Q5;
            Q5=makeQuery(id+"F8.boolean.opBoolean","INTERSECT",EDGE,{"disambiguationData":[OD(0.0)],"derivedFrom":[makeQuery(id+"F5.opExtrude","SWEPT_FACE",FACE,{"disambiguationData":[OSD([sQuery(id+"F4.wireOp",EDGE,"E30")])]}),makeQuery(id+"F8.opExtrude","SWEPT_FACE",FACE,{"disambiguationData":[OSD([sQuery(id+"F7.wireOp",EDGE,"E67")])]})]});
            fillet(context, id + "F14", {"entities" : qUnion([Q0, Q1, Q2, Q3, Q4, Q5]), "radius" : 3 * mm, "tangentPropagation" : true, "allowEdgeOverflow" : false});
        }
        {
            var Q0;
            Q0=makeQuery(id+"F1.opExtrude","CAP_EDGE",EDGE,{"disambiguationData":[OSD([sQuery(id+"F0.wireOp",EDGE,"E1.bottom")])],"isStart":false});
            fillet(context, id + "F15", {"entities" : qUnion([Q0]), "radius" : 2 * mm, "tangentPropagation" : true, "allowEdgeOverflow" : false});
        }
        {
            var Q0;
            {var subQ0=sQuery(id+"F0.wireOp",EDGE,"E21.filletArc");var subQ1=sQuery(id+"F0.wireOp",EDGE,"E7");var subQ2=sQuery(id+"F0.wireOp",EDGE,"E6");var subQ3=sQuery(id+"F0.wireOp",EDGE,"E5");var subQ4=sQuery(id+"F0.wireOp",EDGE,"E4");var subQ5=sQuery(id+"F0.wireOp",EDGE,"E22.filletArc");var subQ6=sQuery(id+"F0.wireOp",EDGE,"E1.bottom");var subQ7=sQuery(id+"F0.wireOp",EDGE,"E1.right");var subQ8=sQuery(id+"F0.wireOp",EDGE,"E1.top");var subQ9=sQuery(id+"F0.wireOp",EDGE,"E1.left");var subQ10=sQuery(id+"F0.wireOp",EDGE,"E23.filletArc");var subQ11=sQuery(id+"F0.wireOp",EDGE,"E24.filletArc");Q0=makeQuery(id+"F2.boolean.opBoolean","SPLIT",FACE,{"disambiguationData":[TD([makeQuery(id+"F1.opExtrude","SWEPT_FACE",FACE,{"disambiguationData":[OSD([subQ6])]})])],"derivedFrom":makeQuery(id+"F1.opExtrude","CAP_FACE",FACE,{"disambiguationData":[OSD([subQ6,subQ8,subQ9,subQ7,subQ4,subQ3,subQ2,subQ1,subQ0,subQ5,subQ10,subQ11])],"isStart":true})});}
            var sketch = newSketch(context, id + "F16", { "sketchPlane" : qUnion([Q0])});
            skLineSegment(sketch, "E79", {"start": v(-33.07, 90) * mm, "end": v(-15.07, 108) * mm});
            skCircle(sketch, "E80", {"center": v(0, 120) * mm, "radius": 6 * mm});
            skArc(sketch, "E81", {"start": v(15, 120) * mm, "mid": v(0, 135) * mm, "end": v(-15, 120) * mm});
            skLineSegment(sketch, "E82", {"start": v(-15, 120) * mm, "end": v(-15.07, 108) * mm});
            skLineSegment(sketch, "E83", {"start": v(15, 120) * mm, "end": v(15, 108) * mm});
            skLineSegment(sketch, "E84", {"start": v(-33.07, 90) * mm, "end": v(33, 90) * mm});
            skLineSegment(sketch, "E85", {"start": v(33, 90) * mm, "end": v(15, 108) * mm});
            skLineSegment(sketch, "E86", {"start": v(-80, 0) * mm, "end": v(80, 0) * mm, "construction": true});
            skLineSegment(sketch, "E87.MirrorCS", {"start": v(-15, -120) * mm, "end": v(-15.07, -108) * mm});
            skLineSegment(sketch, "E88.MirrorCS", {"start": v(15, -120) * mm, "end": v(15, -108) * mm});
            skLineSegment(sketch, "E89.MirrorCS", {"start": v(33, -90) * mm, "end": v(15, -108) * mm});
            skArc(sketch, "E90.MirrorCS", {"start": v(15, -120) * mm, "mid": v(0, -135) * mm, "end": v(-15, -120) * mm});
            skLineSegment(sketch, "E91.MirrorCS", {"start": v(-33.07, -90) * mm, "end": v(33, -90) * mm});
            skLineSegment(sketch, "E92.MirrorCS", {"start": v(-33.07, -90) * mm, "end": v(-15.07, -108) * mm});
            skCircle(sketch, "E93.MirrorC", {"center": v(0, -120) * mm, "radius": 6 * mm});
            skSolve(sketch);
        }
        {
            var Q0;
            Q0=makeQuery(id+"F16.imprint","IMPRINT",FACE,{"disambiguationData":[TD([[makeQuery(id+"F16.imprint","IMPRINT",EDGE,{"derivedFrom":sQuery(id+"F16.wireOp",EDGE,"E79")}),-1.0]])]});
            var Q1;
            {var subQ4=sQuery(id+"F16.wireOp",EDGE,"E84");Q1=makeQuery(id+"F16.imprint","IMPRINT",FACE,{"disambiguationData":[TD([[makeQuery(id+"F16.imprint","IMPRINT",EDGE,{"derivedFrom":subQ4}),-1.0]])]});}
            var Q2;
            Q2=makeQuery(id+"F16.imprint","IMPRINT",FACE,{"disambiguationData":[TD([[makeQuery(id+"F16.imprint","IMPRINT",EDGE,{"derivedFrom":sQuery(id+"F16.wireOp",EDGE,"E87.MirrorCS")}),-1.0]])]});
            var Q3;
            Q3=makeQuery(id+"F2.opExtrude","CAP_FACE",FACE,{"disambiguationData":[OSD([sQuery(id+"F0.wireOp",EDGE,"E12"),sQuery(id+"F0.wireOp",EDGE,"E13"),sQuery(id+"F0.wireOp",EDGE,"E14"),sQuery(id+"F0.wireOp",EDGE,"E15"),sQuery(id+"F0.wireOp",EDGE,"E17.filletArc"),sQuery(id+"F0.wireOp",EDGE,"E18.filletArc"),sQuery(id+"F0.wireOp",EDGE,"E19.filletArc"),sQuery(id+"F0.wireOp",EDGE,"E20.filletArc"),sQuery(id+"F0.wireOp",EDGE,"E25.0"),sQuery(id+"F0.wireOp",EDGE,"E25.1"),sQuery(id+"F0.wireOp",EDGE,"E25.2"),sQuery(id+"F0.wireOp",EDGE,"E25.3"),sQuery(id+"F0.wireOp",EDGE,"E25.4"),sQuery(id+"F0.wireOp",EDGE,"E25.5"),sQuery(id+"F0.wireOp",EDGE,"E25.6"),sQuery(id+"F0.wireOp",EDGE,"E25.7")])],"isStart":false});
            extrude(context, id + "F17", {"entities" : qUnion([Q0, Q1, Q2]), "endBound" : BoundingType.UP_TO_SURFACE, "endBoundEntityFace" : qUnion([Q3]), "depth" : 25 * mm});
        }
    });
